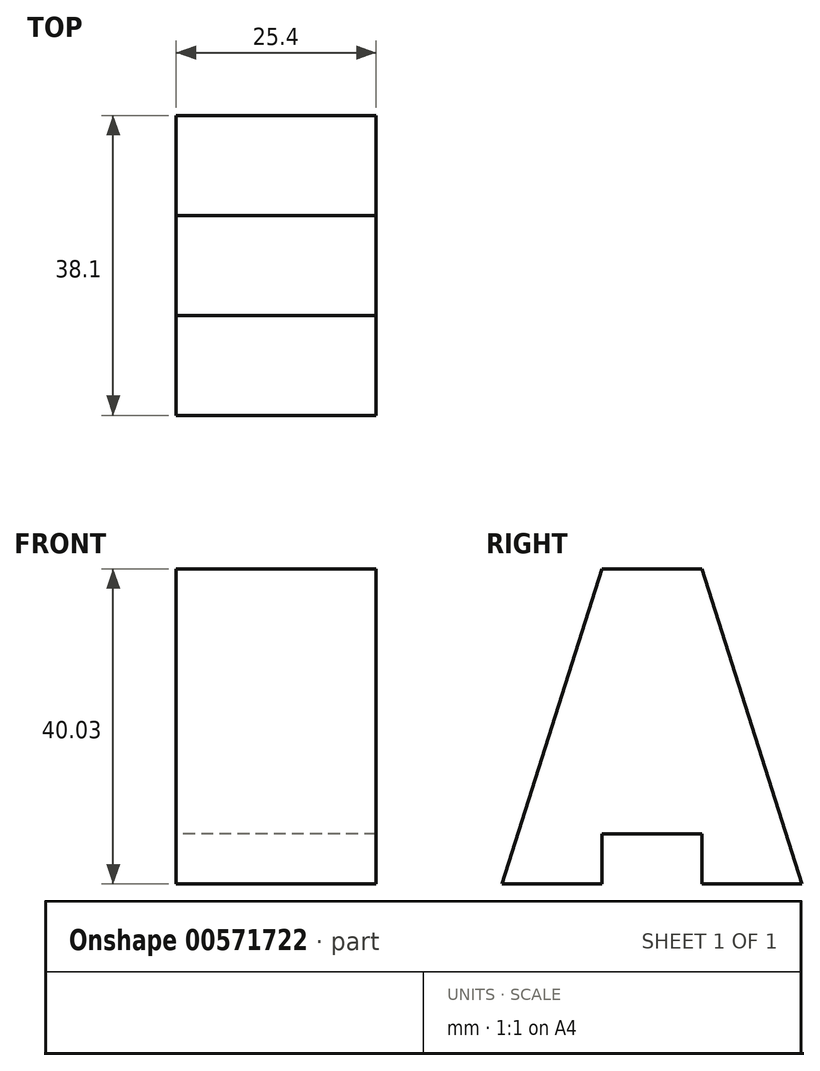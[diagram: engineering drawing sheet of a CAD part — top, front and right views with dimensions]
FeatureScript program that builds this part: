
annotation { "Feature Type Name" : "Feature", "Feature Type Description" : "" }
export const myFeature = defineFeature(function(context is Context, id is Id, definition is map)
    precondition{}
    {
        {
            var Q0;
            Q0=qCreatedBy(makeId("Right.planeOp"),FACE);
            var sketch = newSketch(context, id + "F0", { "sketchPlane" : qUnion([Q0])});
            skLineSegment(sketch, "E0", {"start": v(6.13, 0) * mm, "end": v(-6.57, 0) * mm});
            skLineSegment(sketch, "E1", {"start": v(-6.57, 0) * mm, "end": v(-6.57, -6.35) * mm});
            skLineSegment(sketch, "E2", {"start": v(-6.57, -6.35) * mm, "end": v(-19.27, -6.35) * mm});
            skLineSegment(sketch, "E3", {"start": v(-19.27, -6.35) * mm, "end": v(-6.57, 33.68) * mm});
            skLineSegment(sketch, "E4", {"start": v(-6.57, 33.68) * mm, "end": v(6.13, 33.68) * mm});
            skLineSegment(sketch, "E5", {"start": v(6.13, 33.68) * mm, "end": v(18.83, -6.35) * mm});
            skLineSegment(sketch, "E6", {"start": v(18.83, -6.35) * mm, "end": v(6.13, -6.35) * mm});
            skLineSegment(sketch, "E7", {"start": v(6.13, -6.35) * mm, "end": v(6.13, 0) * mm});
            skSolve(sketch);
        }
        {
            var Q0;
            Q0=makeQuery(id+"F0.imprint","IMPRINT",FACE,{"disambiguationData":[TD([[makeQuery(id+"F0.imprint","IMPRINT",EDGE,{"derivedFrom":sQuery(id+"F0.wireOp",EDGE,"E0")}),-1.0]])]});
            extrude(context, id + "F1", {"entities" : qUnion([Q0]), "depth" : 25.4 * mm, "offsetDistance" : 25.4 * mm});
        }
    });
